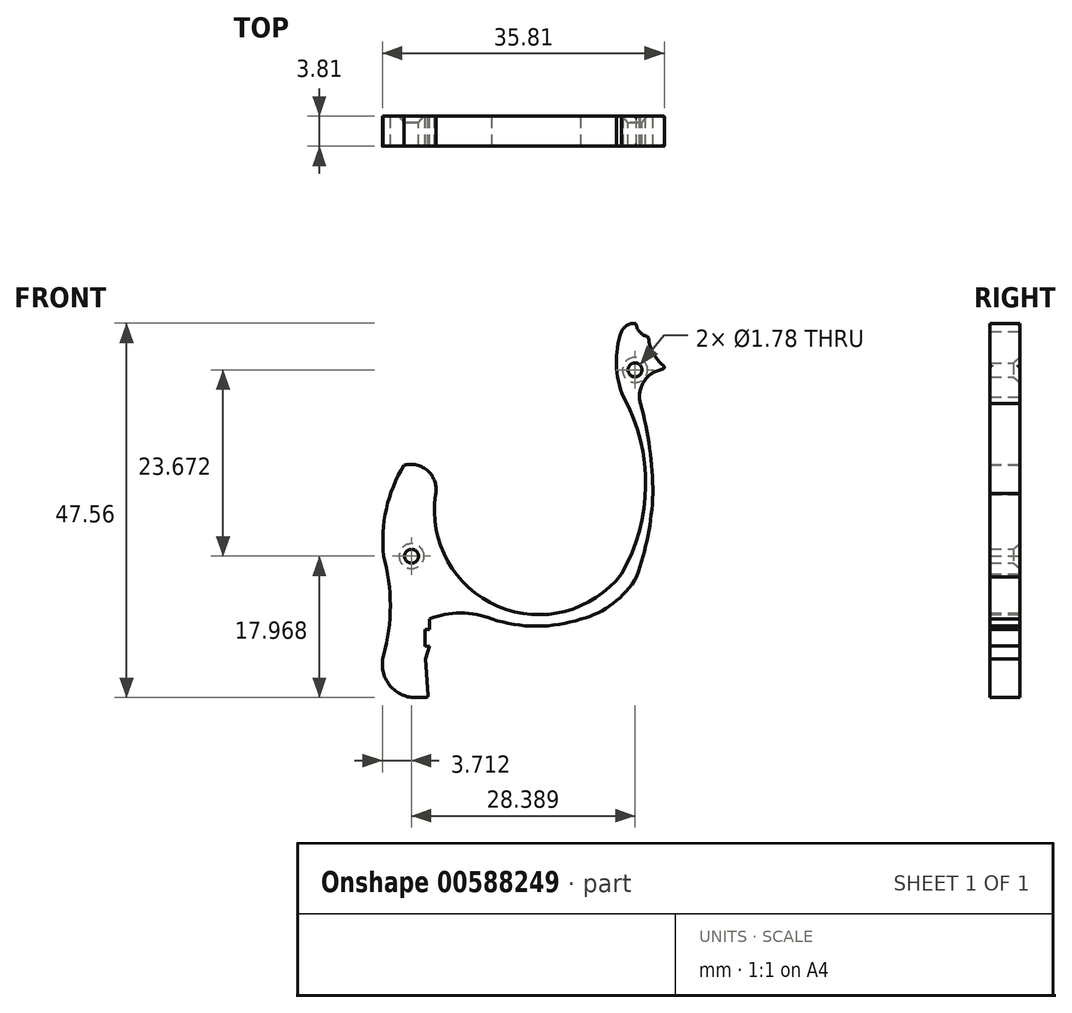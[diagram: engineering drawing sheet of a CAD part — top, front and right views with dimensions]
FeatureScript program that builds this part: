
annotation { "Feature Type Name" : "Feature", "Feature Type Description" : "" }
export const myFeature = defineFeature(function(context is Context, id is Id, definition is map)
    precondition{}
    {
        {
            var Q0;
            Q0=qCreatedBy(makeId("Front.planeOp"),FACE);
            var sketch = newSketch(context, id + "F0", { "sketchPlane" : qUnion([Q0])});
            skArc(sketch, "E0", {"start": v(-15.69, 7.63) * mm, "mid": v(-12.62, 18.81) * mm, "end": v(-15.4, 30.08) * mm});
            skArc(sketch, "E1", {"start": v(-39.29, 17.7) * mm, "mid": v(-31.4, 3.51) * mm, "end": v(-15.69, 7.63) * mm});
            skArc(sketch, "E2", {"start": v(-15.69, 38.42) * mm, "mid": v(-16.34, 34.22) * mm, "end": v(-15.4, 30.08) * mm});
            skArc(sketch, "E3", {"start": v(-43.31, 21.44) * mm, "mid": v(-45.54, 15.9) * mm, "end": v(-45.9, 9.93) * mm});
            skArc(sketch, "E4", {"start": v(-45.9, -2.73) * mm, "mid": v(-45.03, 3.6) * mm, "end": v(-45.9, 9.93) * mm});
            skArc(sketch, "E5", {"start": v(-45.9, -2.73) * mm, "mid": v(-45.13, -6.52) * mm, "end": v(-41.59, -8.08) * mm});
            skPoint(sketch, "E6", {"position": v(-22.6, -2.16) * mm});
            skArc(sketch, "E7", {"start": v(-39.29, 17.7) * mm, "mid": v(-40.25, 20.7) * mm, "end": v(-43.31, 21.44) * mm});
            skPoint(sketch, "E8", {"position": v(-5.35, 30.58) * mm});
            skPoint(sketch, "E9", {"position": v(-9.12, 9) * mm});
            skPoint(sketch, "E10", {"position": v(-32.74, -4.74) * mm});
            skPoint(sketch, "E11.startSnap0", {"position": v(-11.26, 17.15) * mm});
            skArc(sketch, "E12", {"start": v(-32.15, 1.9) * mm, "mid": v(-26.47, 1) * mm, "end": v(-20.8, 1.9) * mm});
            skArc(sketch, "E13", {"start": v(-20.8, 1.9) * mm, "mid": v(-16.73, 3.87) * mm, "end": v(-13.74, 7.27) * mm});
            skArc(sketch, "E14", {"start": v(-13.83, 39.46) * mm, "mid": v(-14.92, 39.23) * mm, "end": v(-15.69, 38.42) * mm});
            skArc(sketch, "E15", {"start": v(-13.83, 39.46) * mm, "mid": v(-13.35, 38.34) * mm, "end": v(-12.27, 37.77) * mm});
            skArc(sketch, "E16", {"start": v(-12.27, 37.77) * mm, "mid": v(-11.51, 35.44) * mm, "end": v(-9.8, 33.69) * mm});
            skLineSegment(sketch, "E17", {"start": v(-41.59, -8.08) * mm, "end": v(-40.23, -8.08) * mm});
            skLineSegment(sketch, "E18", {"start": v(-40.08, 1.9) * mm, "end": v(-40.08, 0.6) * mm});
            skLineSegment(sketch, "E19", {"start": v(-40.08, 0.6) * mm, "end": v(-40.64, 0.6) * mm});
            skLineSegment(sketch, "E20", {"start": v(-40.64, 0.6) * mm, "end": v(-40.64, -1.56) * mm});
            skLineSegment(sketch, "E21", {"start": v(-40.64, -1.56) * mm, "end": v(-40.08, -1.52) * mm});
            skLineSegment(sketch, "E22", {"start": v(-40.08, -1.52) * mm, "end": v(-40.58, -3.2) * mm});
            skArc(sketch, "E23", {"start": v(-32.15, 1.9) * mm, "mid": v(-36.12, 2.67) * mm, "end": v(-40.08, 1.9) * mm});
            skLineSegment(sketch, "E24", {"start": v(-40.23, -8.08) * mm, "end": v(-40.58, -3.2) * mm});
            skArc(sketch, "E25", {"start": v(-9.8, 33.69) * mm, "mid": v(-12.63, 32.33) * mm, "end": v(-13.27, 29.26) * mm});
            skPoint(sketch, "E25.endSnap0", {"position": v(-12.78, 29.26) * mm});
            skArc(sketch, "E26", {"start": v(-11.68, 17.82) * mm, "mid": v(-12.1, 23.6) * mm, "end": v(-13.27, 29.26) * mm});
            skArc(sketch, "E27", {"start": v(-13.74, 7.27) * mm, "mid": v(-12.32, 12.47) * mm, "end": v(-11.68, 17.82) * mm});
            skPoint(sketch, "E28", {"position": v(-42.35, 9.88) * mm});
            skPoint(sketch, "E29", {"position": v(-13.96, 33.55) * mm});
            skSolve(sketch);
        }
        {
            var Q0;
            Q0=makeQuery(id+"F0.imprint","IMPRINT",FACE,{"disambiguationData":[TD([[makeQuery(id+"F0.imprint","IMPRINT",EDGE,{"derivedFrom":sQuery(id+"F0.wireOp",EDGE,"E0")}),-1.0]])]});
            extrude(context, id + "F1", {"entities" : qUnion([Q0]), "depth" : 3.8 * mm, "offsetDistance" : 25.4 * mm});
        }
        {
            var Q0;
            Q0=makeQuery(id+"F1.opExtrude","SWEPT_EDGE",EDGE,{"disambiguationData":[OSD([sQuery(id+"F0.wireOp",EDGE,"E4"),sQuery(id+"F0.wireOp",EDGE,"E5")])]});
            var Q1;
            Q1=makeQuery(id+"F1.opExtrude","SWEPT_EDGE",EDGE,{"disambiguationData":[OSD([sQuery(id+"F0.wireOp",EDGE,"E14"),sQuery(id+"F0.wireOp",EDGE,"E15")])]});
            var Q2;
            Q2=makeQuery(id+"F1.opExtrude","SWEPT_EDGE",EDGE,{"disambiguationData":[OSD([sQuery(id+"F0.wireOp",EDGE,"E15"),sQuery(id+"F0.wireOp",EDGE,"E16")])]});
            var Q3;
            Q3=makeQuery(id+"F1.opExtrude","CAP_EDGE",EDGE,{"disambiguationData":[OSD([sQuery(id+"F0.wireOp",EDGE,"E15")])],"isStart":true});
            var Q4;
            Q4=makeQuery(id+"F1.opExtrude","CAP_EDGE",EDGE,{"disambiguationData":[OSD([sQuery(id+"F0.wireOp",EDGE,"E15")])],"isStart":false});
            var Q5;
            Q5=makeQuery(id+"F1.opExtrude","CAP_EDGE",EDGE,{"disambiguationData":[OSD([sQuery(id+"F0.wireOp",EDGE,"E16")])],"isStart":false});
            var Q6;
            Q6=makeQuery(id+"F1.opExtrude","CAP_EDGE",EDGE,{"disambiguationData":[OSD([sQuery(id+"F0.wireOp",EDGE,"E16")])],"isStart":true});
            var Q7;
            Q7=makeQuery(id+"F1.opExtrude","SWEPT_EDGE",EDGE,{"disambiguationData":[OSD([sQuery(id+"F0.wireOp",EDGE,"vwLTiJYT-6sch-8rlC-inRv-is6fsbZ4HYI5"),sQuery(id+"F0.wireOp",EDGE,"E16")])]});
            var Q8;
            Q8=makeQuery(id+"F1.opExtrude","SWEPT_EDGE",EDGE,{"disambiguationData":[OSD([sQuery(id+"F0.wireOp",EDGE,"E17"),sQuery(id+"F0.wireOp",EDGE,"CpCvzsUK-brAK-I2Sv-0zya-m9kuoP9UWgnK")])]});
            fillet(context, id + "F2", {"entities" : qUnion([Q0, Q1, Q2, Q3, Q4, Q5, Q6, Q7, Q8]), "radius" : 0.25 * mm, "tangentPropagation" : true, "allowEdgeOverflow" : false});
        }
        {
            var Q0;
            Q0=sQuery(id+"F0.wireOp",VERTEX,"11549b07-c463-45e0-93be-ad8b59e47215");
            var Q1;
            Q1=sQuery(id+"F0.wireOp",VERTEX,"c4fa0e8c-e75c-41b4-b291-4c961d96616f");
            var Q2;
            Q2=sQuery(id+"F0.wireOp",VERTEX,"8bc30d14-e7f6-42a1-93c3-a703b894b274");
            var Q3;
            Q3=sQuery(id+"F0.wireOp",VERTEX,"E28");
            var Q4;
            Q4=sQuery(id+"F0.wireOp",VERTEX,"E29");
            var Q5;
            Q5=makeQuery(id+"F1.opExtrude","SWEPT_BODY",BODY,{"disambiguationData":[OSD([sQuery(id+"F0.wireOp",EDGE,"E0"),sQuery(id+"F0.wireOp",EDGE,"E1"),sQuery(id+"F0.wireOp",EDGE,"E2"),sQuery(id+"F0.wireOp",EDGE,"E3"),sQuery(id+"F0.wireOp",EDGE,"E4"),sQuery(id+"F0.wireOp",EDGE,"E5"),sQuery(id+"F0.wireOp",EDGE,"E7"),sQuery(id+"F0.wireOp",EDGE,"E12"),sQuery(id+"F0.wireOp",EDGE,"E13"),sQuery(id+"F0.wireOp",EDGE,"E14"),sQuery(id+"F0.wireOp",EDGE,"E15"),sQuery(id+"F0.wireOp",EDGE,"E16"),sQuery(id+"F0.wireOp",EDGE,"E17"),sQuery(id+"F0.wireOp",EDGE,"E18"),sQuery(id+"F0.wireOp",EDGE,"E19"),sQuery(id+"F0.wireOp",EDGE,"E20"),sQuery(id+"F0.wireOp",EDGE,"E21"),sQuery(id+"F0.wireOp",EDGE,"E22"),sQuery(id+"F0.wireOp",EDGE,"E23"),sQuery(id+"F0.wireOp",EDGE,"E24"),sQuery(id+"F0.wireOp",EDGE,"E25"),sQuery(id+"F0.wireOp",EDGE,"E26"),sQuery(id+"F0.wireOp",EDGE,"E27")])]});
            hole(context, id + "F3", {"style" : HoleStyle.C_SINK, "endStyle" : HoleEndStyle.THROUGH, "oppositeDirection" : true, "holeDiameter" : 1.78 * mm, "cSinkDiameter" : 3.17 * mm, "cSinkAngle" : 82 * degree, "majorDiameter" : 6.35 * mm, "isTappedThrough" : true, "tappedDepth" : 12.7 * mm, "tapClearance" : 3, "locations" : qUnion([Q0, Q1, Q2, Q3, Q4]), "scope" : qUnion([Q5])});
        }
    });
